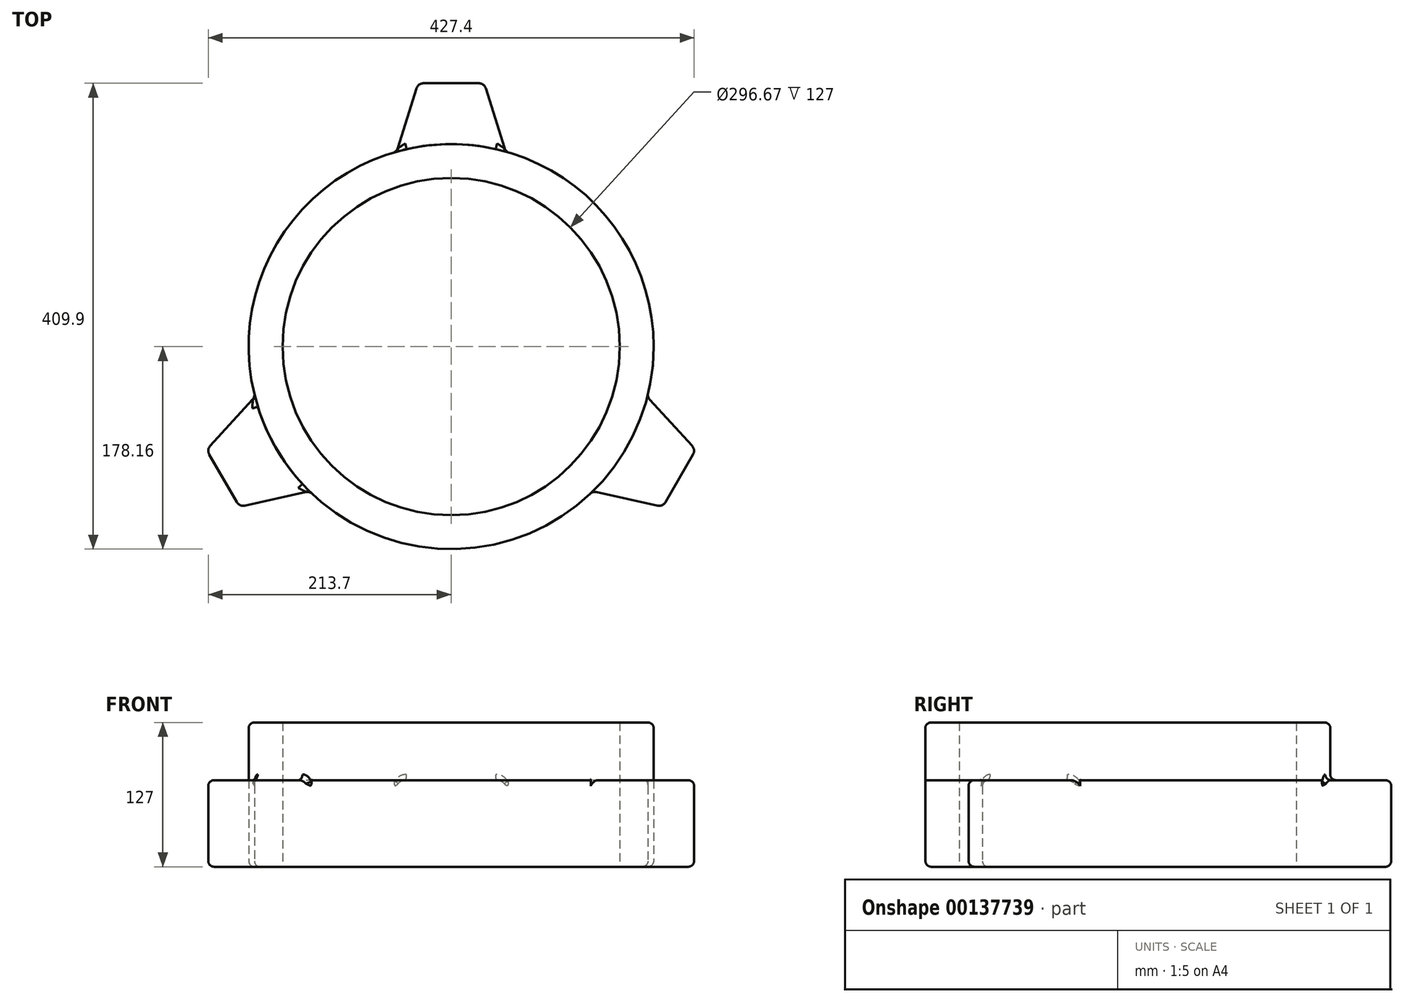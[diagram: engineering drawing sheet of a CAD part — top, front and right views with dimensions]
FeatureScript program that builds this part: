
annotation { "Feature Type Name" : "Feature", "Feature Type Description" : "" }
export const myFeature = defineFeature(function(context is Context, id is Id, definition is map)
    precondition{}
    {
        {
            var Q0;
            Q0=qCreatedBy(makeId("Top.planeOp"),FACE);
            var sketch = newSketch(context, id + "F0", { "sketchPlane" : qUnion([Q0])});
            skCircle(sketch, "E0", {"center": v(0, 0) * mm, "radius": 148.34 * mm});
            skArc(sketch, "E1", {"start": v(-51.2, 170.54) * mm, "mid": v(-154.2, 89.03) * mm, "end": v(-173.3, -40.92) * mm});
            skLineSegment(sketch, "E2", {"start": v(0, 178.06) * mm, "end": v(0, 231.74) * mm, "construction": true});
            skLineSegment(sketch, "E3", {"start": v(0, 231.74) * mm, "end": v(-24.3, 231.74) * mm});
            skLineSegment(sketch, "E4", {"start": v(-30.36, 227.3) * mm, "end": v(-46.98, 174.71) * mm});
            skLineSegment(sketch, "E5.MirrorCS", {"start": v(0, 231.74) * mm, "end": v(24.3, 231.74) * mm});
            skLineSegment(sketch, "E6.MirrorCS", {"start": v(30.36, 227.3) * mm, "end": v(46.98, 174.71) * mm});
            skLineSegment(sketch, "E7.1.0", {"start": v(-200.7, -115.87) * mm, "end": v(-188.54, -136.92) * mm});
            skLineSegment(sketch, "E7.1.1", {"start": v(-200.7, -115.87) * mm, "end": v(-212.85, -94.82) * mm});
            skLineSegment(sketch, "E7.1.2", {"start": v(-212.03, -87.36) * mm, "end": v(-174.8, -46.67) * mm});
            skLineSegment(sketch, "E7.1.3", {"start": v(-181.67, -139.95) * mm, "end": v(-127.81, -128.04) * mm});
            skLineSegment(sketch, "E7.2.0", {"start": v(200.7, -115.87) * mm, "end": v(212.85, -94.82) * mm});
            skLineSegment(sketch, "E7.2.1", {"start": v(200.7, -115.87) * mm, "end": v(188.54, -136.92) * mm});
            skLineSegment(sketch, "E7.2.2", {"start": v(181.67, -139.95) * mm, "end": v(127.81, -128.04) * mm});
            skLineSegment(sketch, "E7.2.3", {"start": v(212.03, -87.36) * mm, "end": v(174.8, -46.67) * mm});
            skArc(sketch, "E8.trimOffspring", {"start": v(173.3, -40.92) * mm, "mid": v(154.2, 89.03) * mm, "end": v(51.2, 170.54) * mm});
            skArc(sketch, "E9.trimOffspring", {"start": v(-122.09, -129.62) * mm, "mid": v(0, -178.06) * mm, "end": v(122.09, -129.62) * mm});
            skPoint(sketch, "E10.visualSharp", {"position": v(-48, 171.47) * mm});
            skArc(sketch, "E10.filletArc", {"start": v(-51.2, 170.54) * mm, "mid": v(-48.58, 172.1) * mm, "end": v(-46.98, 174.71) * mm});
            skPoint(sketch, "E11.visualSharp", {"position": v(-28.96, 231.74) * mm});
            skArc(sketch, "E11.filletArc", {"start": v(-24.3, 231.74) * mm, "mid": v(-28.06, 230.51) * mm, "end": v(-30.36, 227.3) * mm});
            skPoint(sketch, "E12.visualSharp", {"position": v(28.96, 231.74) * mm});
            skArc(sketch, "E12.filletArc", {"start": v(30.36, 227.3) * mm, "mid": v(28.06, 230.51) * mm, "end": v(24.3, 231.74) * mm});
            skPoint(sketch, "E13.visualSharp", {"position": v(48, 171.47) * mm});
            skArc(sketch, "E13.filletArc", {"start": v(46.98, 174.71) * mm, "mid": v(48.58, 172.1) * mm, "end": v(51.2, 170.54) * mm});
            skPoint(sketch, "E14.visualSharp", {"position": v(172.5, -44.16) * mm});
            skArc(sketch, "E14.filletArc", {"start": v(173.3, -40.92) * mm, "mid": v(173.33, -43.98) * mm, "end": v(174.8, -46.67) * mm});
            skPoint(sketch, "E15.visualSharp", {"position": v(215.17, -90.79) * mm});
            skArc(sketch, "E15.filletArc", {"start": v(212.85, -94.82) * mm, "mid": v(213.66, -90.95) * mm, "end": v(212.03, -87.36) * mm});
            skPoint(sketch, "E16.visualSharp", {"position": v(186.21, -140.95) * mm});
            skArc(sketch, "E16.filletArc", {"start": v(181.67, -139.95) * mm, "mid": v(185.6, -139.56) * mm, "end": v(188.54, -136.92) * mm});
            skPoint(sketch, "E17.visualSharp", {"position": v(124.5, -127.3) * mm});
            skArc(sketch, "E17.filletArc", {"start": v(127.81, -128.04) * mm, "mid": v(124.76, -128.12) * mm, "end": v(122.09, -129.62) * mm});
            skPoint(sketch, "E18.visualSharp", {"position": v(-124.5, -127.3) * mm});
            skArc(sketch, "E18.filletArc", {"start": v(-122.09, -129.62) * mm, "mid": v(-124.76, -128.12) * mm, "end": v(-127.81, -128.04) * mm});
            skPoint(sketch, "E19.visualSharp", {"position": v(-186.21, -140.95) * mm});
            skArc(sketch, "E19.filletArc", {"start": v(-188.54, -136.92) * mm, "mid": v(-185.6, -139.56) * mm, "end": v(-181.67, -139.95) * mm});
            skPoint(sketch, "E20.visualSharp", {"position": v(-215.17, -90.79) * mm});
            skArc(sketch, "E20.filletArc", {"start": v(-212.03, -87.36) * mm, "mid": v(-213.66, -90.95) * mm, "end": v(-212.85, -94.82) * mm});
            skPoint(sketch, "E21.visualSharp", {"position": v(-172.5, -44.16) * mm});
            skArc(sketch, "E21.filletArc", {"start": v(-174.8, -46.67) * mm, "mid": v(-173.33, -43.98) * mm, "end": v(-173.3, -40.92) * mm});
            skSolve(sketch);
        }
        {
            var Q0;
            Q0 = qSketchRegion(id + "F0", true);
            extrude(context, id + "F1", {"entities" : qUnion([Q0]), "depth" : 76.2 * mm});
        }
        {
            var Q0;
            Q0=makeQuery(id+"F1.opExtrude","CAP_FACE",FACE,{"disambiguationData":[OSD([sQuery(id+"F0.wireOp",EDGE,"E0"),sQuery(id+"F0.wireOp",EDGE,"E1"),sQuery(id+"F0.wireOp",EDGE,"E3"),sQuery(id+"F0.wireOp",EDGE,"E4"),sQuery(id+"F0.wireOp",EDGE,"E5.MirrorCS"),sQuery(id+"F0.wireOp",EDGE,"E6.MirrorCS"),sQuery(id+"F0.wireOp",EDGE,"E7.1.0"),sQuery(id+"F0.wireOp",EDGE,"E7.1.1"),sQuery(id+"F0.wireOp",EDGE,"E7.1.2"),sQuery(id+"F0.wireOp",EDGE,"E7.1.3"),sQuery(id+"F0.wireOp",EDGE,"E7.2.0"),sQuery(id+"F0.wireOp",EDGE,"E7.2.1"),sQuery(id+"F0.wireOp",EDGE,"E7.2.2"),sQuery(id+"F0.wireOp",EDGE,"E7.2.3"),sQuery(id+"F0.wireOp",EDGE,"E8.trimOffspring"),sQuery(id+"F0.wireOp",EDGE,"E9.trimOffspring"),sQuery(id+"F0.wireOp",EDGE,"E10.filletArc"),sQuery(id+"F0.wireOp",EDGE,"E11.filletArc"),sQuery(id+"F0.wireOp",EDGE,"E12.filletArc"),sQuery(id+"F0.wireOp",EDGE,"E13.filletArc"),sQuery(id+"F0.wireOp",EDGE,"E14.filletArc"),sQuery(id+"F0.wireOp",EDGE,"E15.filletArc"),sQuery(id+"F0.wireOp",EDGE,"E16.filletArc"),sQuery(id+"F0.wireOp",EDGE,"E17.filletArc"),sQuery(id+"F0.wireOp",EDGE,"E18.filletArc"),sQuery(id+"F0.wireOp",EDGE,"E19.filletArc"),sQuery(id+"F0.wireOp",EDGE,"E20.filletArc"),sQuery(id+"F0.wireOp",EDGE,"E21.filletArc")])],"isStart":false});
            var sketch = newSketch(context, id + "F2", { "sketchPlane" : qUnion([Q0])});
            skCircle(sketch, "E22", {"center": v(0, 0) * mm, "radius": 148.34 * mm});
            skCircle(sketch, "E23", {"center": v(0, 0) * mm, "radius": 178.16 * mm});
            skSolve(sketch);
        }
        {
            var Q0;
            Q0 = qSketchRegion(id + "F2", true);
            extrude(context, id + "F3", {"entities" : qUnion([Q0]), "operationType" : NewBodyOperationType.ADD, "depth" : 50.8 * mm});
        }
        {
            var Q0;
            Q0=makeQuery(id+"F1.opExtrude","CAP_EDGE",EDGE,{"disambiguationData":[OSD([sQuery(id+"F0.wireOp",EDGE,"E4")])],"isStart":false});
            var Q1;
            Q1=makeQuery(id+"F1.opExtrude","CAP_EDGE",EDGE,{"disambiguationData":[OSD([sQuery(id+"F0.wireOp",EDGE,"E7.1.2")])],"isStart":false});
            var Q2;
            Q2=makeQuery(id+"F1.opExtrude","CAP_EDGE",EDGE,{"disambiguationData":[OSD([sQuery(id+"F0.wireOp",EDGE,"E7.1.2")])],"isStart":true});
            var Q3;
            Q3=makeQuery(id+"F1.opExtrude","CAP_EDGE",EDGE,{"disambiguationData":[OSD([sQuery(id+"F0.wireOp",EDGE,"E7.2.2")])],"isStart":false});
            var Q4;
            Q4=makeQuery(id+"F3.opExtrude","CAP_EDGE",EDGE,{"disambiguationData":[OSD([sQuery(id+"F2.wireOp",EDGE,"E23")])],"isStart":false});
            fillet(context, id + "F4", {"entities" : qUnion([Q0, Q1, Q2, Q3, Q4]), "radius" : 5.08 * mm, "tangentPropagation" : true, "allowEdgeOverflow" : false});
        }
        {
            var Q0;
            {var subQ0=sQuery(id+"F2.wireOp",EDGE,"E23");var subQ1=sQuery(id+"F0.wireOp",EDGE,"E21.filletArc");var subQ2=sQuery(id+"F0.wireOp",EDGE,"E18.filletArc");Q0=makeQuery(id+"F3.boolean.opBoolean","SPLIT",EDGE,{"disambiguationData":[TD([makeQuery(id+"F1.opExtrude","CAP_FACE",FACE,{"disambiguationData":[OSD([sQuery(id+"F0.wireOp",EDGE,"E0"),sQuery(id+"F0.wireOp",EDGE,"E1"),sQuery(id+"F0.wireOp",EDGE,"E3"),sQuery(id+"F0.wireOp",EDGE,"E4"),sQuery(id+"F0.wireOp",EDGE,"E5.MirrorCS"),sQuery(id+"F0.wireOp",EDGE,"E6.MirrorCS"),sQuery(id+"F0.wireOp",EDGE,"E7.1.0"),sQuery(id+"F0.wireOp",EDGE,"E7.1.1"),sQuery(id+"F0.wireOp",EDGE,"E7.1.2"),sQuery(id+"F0.wireOp",EDGE,"E7.1.3"),sQuery(id+"F0.wireOp",EDGE,"E7.2.0"),sQuery(id+"F0.wireOp",EDGE,"E7.2.1"),sQuery(id+"F0.wireOp",EDGE,"E7.2.2"),sQuery(id+"F0.wireOp",EDGE,"E7.2.3"),sQuery(id+"F0.wireOp",EDGE,"E8.trimOffspring"),sQuery(id+"F0.wireOp",EDGE,"E9.trimOffspring"),sQuery(id+"F0.wireOp",EDGE,"E10.filletArc"),sQuery(id+"F0.wireOp",EDGE,"E11.filletArc"),sQuery(id+"F0.wireOp",EDGE,"E12.filletArc"),sQuery(id+"F0.wireOp",EDGE,"E13.filletArc"),sQuery(id+"F0.wireOp",EDGE,"E14.filletArc"),sQuery(id+"F0.wireOp",EDGE,"E15.filletArc"),sQuery(id+"F0.wireOp",EDGE,"E16.filletArc"),sQuery(id+"F0.wireOp",EDGE,"E17.filletArc"),subQ2,sQuery(id+"F0.wireOp",EDGE,"E19.filletArc"),sQuery(id+"F0.wireOp",EDGE,"E20.filletArc"),subQ1])],"isStart":false}),makeQuery(id+"F1.opExtrude","SWEPT_FACE",FACE,{"disambiguationData":[OSD([subQ2])]}),makeQuery(id+"F1.opExtrude","SWEPT_FACE",FACE,{"disambiguationData":[OSD([subQ1])]}),makeQuery(id+"F3.opExtrude","CAP_FACE",FACE,{"disambiguationData":[OSD([sQuery(id+"F2.wireOp",EDGE,"E22"),subQ0])],"isStart":true}),makeQuery(id+"F3.opExtrude","SWEPT_FACE",FACE,{"disambiguationData":[OSD([subQ0])]})])],"derivedFrom":makeQuery(id+"F3.opExtrude","CAP_EDGE",EDGE,{"disambiguationData":[OSD([subQ0])],"isStart":true})});}
            var Q1;
            {var subQ0=sQuery(id+"F0.wireOp",EDGE,"E17.filletArc");var subQ1=sQuery(id+"F0.wireOp",EDGE,"E14.filletArc");var subQ2=sQuery(id+"F2.wireOp",EDGE,"E23");Q1=makeQuery(id+"F3.boolean.opBoolean","SPLIT",EDGE,{"disambiguationData":[TD([makeQuery(id+"F1.opExtrude","CAP_FACE",FACE,{"disambiguationData":[OSD([sQuery(id+"F0.wireOp",EDGE,"E0"),sQuery(id+"F0.wireOp",EDGE,"E1"),sQuery(id+"F0.wireOp",EDGE,"E3"),sQuery(id+"F0.wireOp",EDGE,"E4"),sQuery(id+"F0.wireOp",EDGE,"E5.MirrorCS"),sQuery(id+"F0.wireOp",EDGE,"E6.MirrorCS"),sQuery(id+"F0.wireOp",EDGE,"E7.1.0"),sQuery(id+"F0.wireOp",EDGE,"E7.1.1"),sQuery(id+"F0.wireOp",EDGE,"E7.1.2"),sQuery(id+"F0.wireOp",EDGE,"E7.1.3"),sQuery(id+"F0.wireOp",EDGE,"E7.2.0"),sQuery(id+"F0.wireOp",EDGE,"E7.2.1"),sQuery(id+"F0.wireOp",EDGE,"E7.2.2"),sQuery(id+"F0.wireOp",EDGE,"E7.2.3"),sQuery(id+"F0.wireOp",EDGE,"E8.trimOffspring"),sQuery(id+"F0.wireOp",EDGE,"E9.trimOffspring"),sQuery(id+"F0.wireOp",EDGE,"E10.filletArc"),sQuery(id+"F0.wireOp",EDGE,"E11.filletArc"),sQuery(id+"F0.wireOp",EDGE,"E12.filletArc"),sQuery(id+"F0.wireOp",EDGE,"E13.filletArc"),subQ1,sQuery(id+"F0.wireOp",EDGE,"E15.filletArc"),sQuery(id+"F0.wireOp",EDGE,"E16.filletArc"),subQ0,sQuery(id+"F0.wireOp",EDGE,"E18.filletArc"),sQuery(id+"F0.wireOp",EDGE,"E19.filletArc"),sQuery(id+"F0.wireOp",EDGE,"E20.filletArc"),sQuery(id+"F0.wireOp",EDGE,"E21.filletArc")])],"isStart":false}),makeQuery(id+"F1.opExtrude","SWEPT_FACE",FACE,{"disambiguationData":[OSD([subQ1])]}),makeQuery(id+"F1.opExtrude","SWEPT_FACE",FACE,{"disambiguationData":[OSD([subQ0])]}),makeQuery(id+"F3.opExtrude","CAP_FACE",FACE,{"disambiguationData":[OSD([sQuery(id+"F2.wireOp",EDGE,"E22"),subQ2])],"isStart":true}),makeQuery(id+"F3.opExtrude","SWEPT_FACE",FACE,{"disambiguationData":[OSD([subQ2])]})])],"derivedFrom":makeQuery(id+"F3.opExtrude","CAP_EDGE",EDGE,{"disambiguationData":[OSD([subQ2])],"isStart":true})});}
            var Q2;
            {var subQ0=sQuery(id+"F2.wireOp",EDGE,"E23");var subQ1=sQuery(id+"F0.wireOp",EDGE,"E10.filletArc");var subQ2=sQuery(id+"F0.wireOp",EDGE,"E13.filletArc");Q2=makeQuery(id+"F3.boolean.opBoolean","SPLIT",EDGE,{"disambiguationData":[TD([makeQuery(id+"F1.opExtrude","CAP_FACE",FACE,{"disambiguationData":[OSD([sQuery(id+"F0.wireOp",EDGE,"E0"),sQuery(id+"F0.wireOp",EDGE,"E1"),sQuery(id+"F0.wireOp",EDGE,"E3"),sQuery(id+"F0.wireOp",EDGE,"E4"),sQuery(id+"F0.wireOp",EDGE,"E5.MirrorCS"),sQuery(id+"F0.wireOp",EDGE,"E6.MirrorCS"),sQuery(id+"F0.wireOp",EDGE,"E7.1.0"),sQuery(id+"F0.wireOp",EDGE,"E7.1.1"),sQuery(id+"F0.wireOp",EDGE,"E7.1.2"),sQuery(id+"F0.wireOp",EDGE,"E7.1.3"),sQuery(id+"F0.wireOp",EDGE,"E7.2.0"),sQuery(id+"F0.wireOp",EDGE,"E7.2.1"),sQuery(id+"F0.wireOp",EDGE,"E7.2.2"),sQuery(id+"F0.wireOp",EDGE,"E7.2.3"),sQuery(id+"F0.wireOp",EDGE,"E8.trimOffspring"),sQuery(id+"F0.wireOp",EDGE,"E9.trimOffspring"),subQ1,sQuery(id+"F0.wireOp",EDGE,"E11.filletArc"),sQuery(id+"F0.wireOp",EDGE,"E12.filletArc"),subQ2,sQuery(id+"F0.wireOp",EDGE,"E14.filletArc"),sQuery(id+"F0.wireOp",EDGE,"E15.filletArc"),sQuery(id+"F0.wireOp",EDGE,"E16.filletArc"),sQuery(id+"F0.wireOp",EDGE,"E17.filletArc"),sQuery(id+"F0.wireOp",EDGE,"E18.filletArc"),sQuery(id+"F0.wireOp",EDGE,"E19.filletArc"),sQuery(id+"F0.wireOp",EDGE,"E20.filletArc"),sQuery(id+"F0.wireOp",EDGE,"E21.filletArc")])],"isStart":false}),makeQuery(id+"F1.opExtrude","SWEPT_FACE",FACE,{"disambiguationData":[OSD([subQ1])]}),makeQuery(id+"F1.opExtrude","SWEPT_FACE",FACE,{"disambiguationData":[OSD([subQ2])]}),makeQuery(id+"F3.opExtrude","CAP_FACE",FACE,{"disambiguationData":[OSD([sQuery(id+"F2.wireOp",EDGE,"E22"),subQ0])],"isStart":true}),makeQuery(id+"F3.opExtrude","SWEPT_FACE",FACE,{"disambiguationData":[OSD([subQ0])]})])],"derivedFrom":makeQuery(id+"F3.opExtrude","CAP_EDGE",EDGE,{"disambiguationData":[OSD([subQ0])],"isStart":true})});}
            fillet(context, id + "F5", {"entities" : qUnion([Q0, Q1, Q2]), "radius" : 5.08 * mm, "tangentPropagation" : true, "allowEdgeOverflow" : false});
        }
    });
